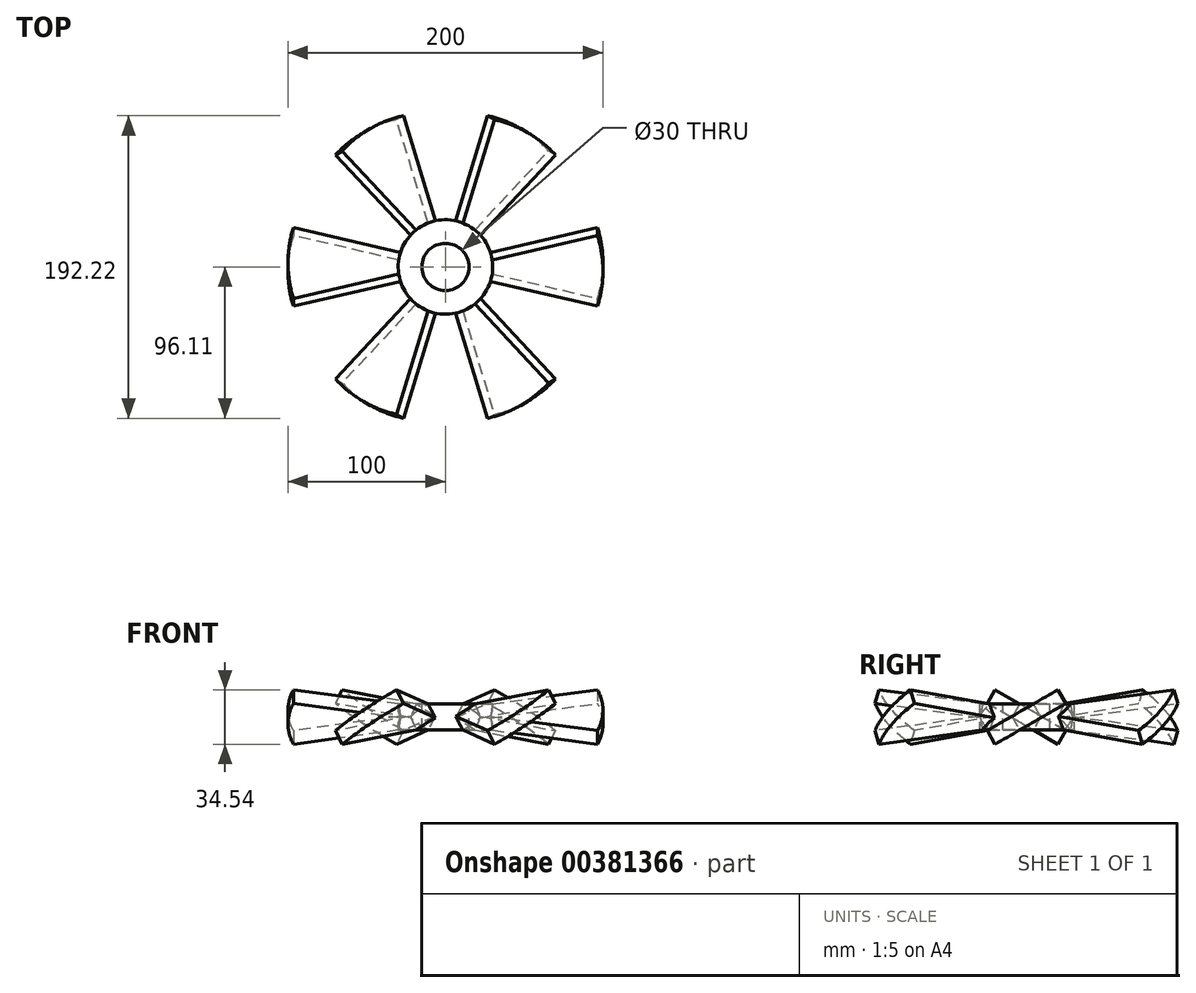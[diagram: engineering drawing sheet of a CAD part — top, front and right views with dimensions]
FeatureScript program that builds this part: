
annotation { "Feature Type Name" : "Feature", "Feature Type Description" : "" }
export const myFeature = defineFeature(function(context is Context, id is Id, definition is map)
    precondition{}
    {
        {
            var Q0;
            Q0=qCreatedBy(makeId("Top.planeOp"),FACE);
            var sketch = newSketch(context, id + "F0", { "sketchPlane" : qUnion([Q0])});
            skLineSegment(sketch, "E0", {"start": v(0, 0) * mm, "end": v(96.6, -25.88) * mm});
            skArc(sketch, "E1", {"start": v(96.6, -25.88) * mm, "mid": v(100, 0) * mm, "end": v(96.6, 25.88) * mm});
            skLineSegment(sketch, "E2", {"start": v(-21.82, 0) * mm, "end": v(117.57, 0) * mm, "construction": true});
            skLineSegment(sketch, "E3.MirrorCS", {"start": v(0, 0) * mm, "end": v(96.6, 25.88) * mm});
            skSolve(sketch);
        }
        {
            var Q0;
            Q0=makeQuery(id+"F0.imprint","IMPRINT",FACE,{"disambiguationData":[TD([[makeQuery(id+"F0.imprint","IMPRINT",EDGE,{"derivedFrom":sQuery(id+"F0.wireOp",EDGE,"E0")}),1.0]])]});
            extrude(context, id + "F1", {"entities" : qUnion([Q0]), "depth" : 5 * mm, "hasSecondDirection" : true, "secondDirectionOppositeDirection" : true, "secondDirectionDepth" : 5 * mm});
        }
        {
            var Q0;
            Q0=qCreatedBy(makeId("Top.planeOp"),FACE);
            var sketch = newSketch(context, id + "F2", { "sketchPlane" : qUnion([Q0])});
            skLineSegment(sketch, "E4", {"start": v(-12.3, 0) * mm, "end": v(109.83, 0) * mm, "construction": true});
            skSolve(sketch);
        }
        {
            var Q0;
            Q0=makeQuery(id+"F1.opExtrude","SWEPT_BODY",BODY,{"disambiguationData":[OSD([sQuery(id+"F0.wireOp",EDGE,"E0"),sQuery(id+"F0.wireOp",EDGE,"E1"),sQuery(id+"F0.wireOp",EDGE,"E3.MirrorCS")])]});
            var Q1;
            Q1=sQuery(id+"F2.wireOp",EDGE,"E4");
            var Q2;
            Q2=sQuery(id+"F2.wireOp",EDGE,"E4");
            transform(context, id + "F3", {"entities" : qUnion([Q0]), "transformType" : TransformType.ROTATION, "transformAxis" : qUnion([Q2]), "angle" : 30 * degree, "makeCopy" : false});
        }
        {
            var Q0;
            Q0=qCreatedBy(makeId("Right.planeOp"),FACE);
            var sketch = newSketch(context, id + "F4", { "sketchPlane" : qUnion([Q0])});
            skLineSegment(sketch, "E5", {"start": v(0, 0) * mm, "end": v(0, 57.38) * mm, "construction": true});
            skSolve(sketch);
        }
        {
            var Q0;
            Q0=makeQuery(id+"F1.opExtrude","SWEPT_BODY",BODY,{"disambiguationData":[OSD([sQuery(id+"F0.wireOp",EDGE,"E0"),sQuery(id+"F0.wireOp",EDGE,"E1"),sQuery(id+"F0.wireOp",EDGE,"E3.MirrorCS")])]});
            var Q1;
            Q1=sQuery(id+"F4.wireOp",EDGE,"E5");
            circularPattern(context, id + "F5", {"entities" : qUnion([Q0]), "axis" : qUnion([Q1]), "angle" : 360 * degree, "instanceCount" : 6, "equalSpace" : true});
        }
        {
            var Q0;
            Q0=qCreatedBy(makeId("Top.planeOp"),FACE);
            var sketch = newSketch(context, id + "F6", { "sketchPlane" : qUnion([Q0])});
            skCircle(sketch, "E6", {"center": v(0, 0) * mm, "radius": 30 * mm});
            skSolve(sketch);
        }
        {
            var Q0;
            Q0=makeQuery(id+"F6.imprint","IMPRINT",FACE,{"disambiguationData":[TD([[makeQuery(id+"F6.imprint","IMPRINT",EDGE,{"derivedFrom":sQuery(id+"F6.wireOp",EDGE,"E6")}),1.0]])]});
            var Q1;
            Q1=sQuery(id+"F6.wireOp",EDGE,"E6");
            extrude(context, id + "F7", {"entities" : qUnion([Q0]), "surfaceEntities" : qUnion([Q1]), "depth" : 25 * mm, "hasSecondDirection" : true, "secondDirectionOppositeDirection" : true, "secondDirectionDepth" : 25 * mm});
        }
        {
            var Q0;
            Q0=makeQuery(id+"F5.opPattern","COPY",BODY,{"derivedFrom":makeQuery(id+"F1.opExtrude","SWEPT_BODY",BODY,{"disambiguationData":[OSD([sQuery(id+"F0.wireOp",EDGE,"E0"),sQuery(id+"F0.wireOp",EDGE,"E1"),sQuery(id+"F0.wireOp",EDGE,"E3.MirrorCS")])]}),"instanceName":"1"});
            var Q1;
            Q1=makeQuery(id+"F5.opPattern","COPY",BODY,{"derivedFrom":makeQuery(id+"F1.opExtrude","SWEPT_BODY",BODY,{"disambiguationData":[OSD([sQuery(id+"F0.wireOp",EDGE,"E0"),sQuery(id+"F0.wireOp",EDGE,"E1"),sQuery(id+"F0.wireOp",EDGE,"E3.MirrorCS")])]}),"instanceName":"3"});
            var Q2;
            Q2=makeQuery(id+"F5.opPattern","COPY",BODY,{"derivedFrom":makeQuery(id+"F1.opExtrude","SWEPT_BODY",BODY,{"disambiguationData":[OSD([sQuery(id+"F0.wireOp",EDGE,"E0"),sQuery(id+"F0.wireOp",EDGE,"E1"),sQuery(id+"F0.wireOp",EDGE,"E3.MirrorCS")])]}),"instanceName":"5"});
            var Q3;
            Q3=makeQuery(id+"F5.opPattern","COPY",BODY,{"derivedFrom":makeQuery(id+"F1.opExtrude","SWEPT_BODY",BODY,{"disambiguationData":[OSD([sQuery(id+"F0.wireOp",EDGE,"E0"),sQuery(id+"F0.wireOp",EDGE,"E1"),sQuery(id+"F0.wireOp",EDGE,"E3.MirrorCS")])]}),"instanceName":"2"});
            var Q4;
            Q4=makeQuery(id+"F5.opPattern","COPY",BODY,{"derivedFrom":makeQuery(id+"F1.opExtrude","SWEPT_BODY",BODY,{"disambiguationData":[OSD([sQuery(id+"F0.wireOp",EDGE,"E0"),sQuery(id+"F0.wireOp",EDGE,"E1"),sQuery(id+"F0.wireOp",EDGE,"E3.MirrorCS")])]}),"instanceName":"4"});
            var Q5;
            Q5=makeQuery(id+"F1.opExtrude","SWEPT_BODY",BODY,{"disambiguationData":[OSD([sQuery(id+"F0.wireOp",EDGE,"E0"),sQuery(id+"F0.wireOp",EDGE,"E1"),sQuery(id+"F0.wireOp",EDGE,"E3.MirrorCS")])]});
            var Q6;
            Q6=makeQuery(id+"F7.opExtrude","SWEPT_BODY",BODY,{"disambiguationData":[OSD([sQuery(id+"F6.wireOp",EDGE,"E6")])]});
            booleanBodies(context, id + "F8", {"operationType" : BooleanOperationType.UNION, "tools" : qUnion([Q0, Q1, Q2, Q3, Q4, Q5, Q6])});
        }
        {
            var Q0;
            {var subQ0=sQuery(id+"F0.wireOp",EDGE,"E0");Q0=makeQuery(id+"F8.opBoolean","INTERSECT",VERTEX,{"derivedFrom":[makeQuery(id+"F5.opPattern","COPY",FACE,{"derivedFrom":makeQuery(id+"F1.opExtrude","SWEPT_FACE",FACE,{"disambiguationData":[OSD([subQ0])]}),"instanceName":"1"}),makeQuery(id+"F5.opPattern","COPY",FACE,{"derivedFrom":makeQuery(id+"F1.opExtrude","CAP_FACE",FACE,{"disambiguationData":[OSD([subQ0,sQuery(id+"F0.wireOp",EDGE,"E1"),sQuery(id+"F0.wireOp",EDGE,"E3.MirrorCS")])],"isStart":true}),"instanceName":"1"}),makeQuery(id+"F7.opExtrude","SWEPT_FACE",FACE,{"disambiguationData":[OSD([sQuery(id+"F6.wireOp",EDGE,"E6")])]})]});}
            var Q1;
            {var subQ0=sQuery(id+"F0.wireOp",EDGE,"E0");Q1=makeQuery(id+"F8.opBoolean","INTERSECT",VERTEX,{"derivedFrom":[makeQuery(id+"F5.opPattern","COPY",FACE,{"derivedFrom":makeQuery(id+"F1.opExtrude","SWEPT_FACE",FACE,{"disambiguationData":[OSD([subQ0])]}),"instanceName":"5"}),makeQuery(id+"F5.opPattern","COPY",FACE,{"derivedFrom":makeQuery(id+"F1.opExtrude","CAP_FACE",FACE,{"disambiguationData":[OSD([subQ0,sQuery(id+"F0.wireOp",EDGE,"E1"),sQuery(id+"F0.wireOp",EDGE,"E3.MirrorCS")])],"isStart":true}),"instanceName":"5"}),makeQuery(id+"F7.opExtrude","SWEPT_FACE",FACE,{"disambiguationData":[OSD([sQuery(id+"F6.wireOp",EDGE,"E6")])]})]});}
            var Q2;
            {var subQ0=sQuery(id+"F0.wireOp",EDGE,"E0");Q2=makeQuery(id+"F8.opBoolean","INTERSECT",VERTEX,{"derivedFrom":[makeQuery(id+"F5.opPattern","COPY",FACE,{"derivedFrom":makeQuery(id+"F1.opExtrude","SWEPT_FACE",FACE,{"disambiguationData":[OSD([subQ0])]}),"instanceName":"3"}),makeQuery(id+"F5.opPattern","COPY",FACE,{"derivedFrom":makeQuery(id+"F1.opExtrude","CAP_FACE",FACE,{"disambiguationData":[OSD([subQ0,sQuery(id+"F0.wireOp",EDGE,"E1"),sQuery(id+"F0.wireOp",EDGE,"E3.MirrorCS")])],"isStart":true}),"instanceName":"3"}),makeQuery(id+"F7.opExtrude","SWEPT_FACE",FACE,{"disambiguationData":[OSD([sQuery(id+"F6.wireOp",EDGE,"E6")])]})]});}
            cPlane(context, id + "F9", {"entities" : qUnion([Q0, Q1, Q2]), "cplaneType" : CPlaneType.THREE_POINT, "offset" : 25 * mm, "width" : 150 * mm, "height" : 150 * mm});
        }
        {
            var Q0;
            {var subQ0=sQuery(id+"F0.wireOp",EDGE,"E3.MirrorCS");Q0=makeQuery(id+"F8.opBoolean","INTERSECT",VERTEX,{"derivedFrom":[makeQuery(id+"F1.opExtrude","CAP_FACE",FACE,{"disambiguationData":[OSD([sQuery(id+"F0.wireOp",EDGE,"E0"),sQuery(id+"F0.wireOp",EDGE,"E1"),subQ0])],"isStart":false}),makeQuery(id+"F1.opExtrude","SWEPT_FACE",FACE,{"disambiguationData":[OSD([subQ0])]}),makeQuery(id+"F7.opExtrude","SWEPT_FACE",FACE,{"disambiguationData":[OSD([sQuery(id+"F6.wireOp",EDGE,"E6")])]})]});}
            var Q1;
            {var subQ0=sQuery(id+"F0.wireOp",EDGE,"E3.MirrorCS");Q1=makeQuery(id+"F8.opBoolean","INTERSECT",VERTEX,{"derivedFrom":[makeQuery(id+"F5.opPattern","COPY",FACE,{"derivedFrom":makeQuery(id+"F1.opExtrude","CAP_FACE",FACE,{"disambiguationData":[OSD([sQuery(id+"F0.wireOp",EDGE,"E0"),sQuery(id+"F0.wireOp",EDGE,"E1"),subQ0])],"isStart":false}),"instanceName":"1"}),makeQuery(id+"F5.opPattern","COPY",FACE,{"derivedFrom":makeQuery(id+"F1.opExtrude","SWEPT_FACE",FACE,{"disambiguationData":[OSD([subQ0])]}),"instanceName":"1"}),makeQuery(id+"F7.opExtrude","SWEPT_FACE",FACE,{"disambiguationData":[OSD([sQuery(id+"F6.wireOp",EDGE,"E6")])]})]});}
            var Q2;
            {var subQ0=sQuery(id+"F0.wireOp",EDGE,"E3.MirrorCS");Q2=makeQuery(id+"F8.opBoolean","INTERSECT",VERTEX,{"derivedFrom":[makeQuery(id+"F5.opPattern","COPY",FACE,{"derivedFrom":makeQuery(id+"F1.opExtrude","CAP_FACE",FACE,{"disambiguationData":[OSD([sQuery(id+"F0.wireOp",EDGE,"E0"),sQuery(id+"F0.wireOp",EDGE,"E1"),subQ0])],"isStart":false}),"instanceName":"3"}),makeQuery(id+"F5.opPattern","COPY",FACE,{"derivedFrom":makeQuery(id+"F1.opExtrude","SWEPT_FACE",FACE,{"disambiguationData":[OSD([subQ0])]}),"instanceName":"3"}),makeQuery(id+"F7.opExtrude","SWEPT_FACE",FACE,{"disambiguationData":[OSD([sQuery(id+"F6.wireOp",EDGE,"E6")])]})]});}
            cPlane(context, id + "F10", {"entities" : qUnion([Q0, Q1, Q2]), "cplaneType" : CPlaneType.THREE_POINT, "offset" : 25 * mm, "width" : 150 * mm, "height" : 150 * mm});
        }
        {
            var Q0;
            Q0=makeQuery(id+"F7.opExtrude","CAP_FACE",FACE,{"disambiguationData":[OSD([sQuery(id+"F6.wireOp",EDGE,"E6")])],"isStart":true});
            var Q1;
            Q1=qCreatedBy(id+"F9.planeOp",FACE);
            extrude(context, id + "F11", {"entities" : qUnion([Q0]), "operationType" : NewBodyOperationType.REMOVE, "endBound" : BoundingType.UP_TO_SURFACE, "oppositeDirection" : true, "endBoundEntityFace" : qUnion([Q1]), "depth" : 25 * mm});
        }
        {
            var Q0;
            Q0=makeQuery(id+"F7.opExtrude","CAP_FACE",FACE,{"disambiguationData":[OSD([sQuery(id+"F6.wireOp",EDGE,"E6")])],"isStart":false});
            var Q1;
            Q1=qCreatedBy(id+"F10.planeOp",FACE);
            extrude(context, id + "F12", {"entities" : qUnion([Q0]), "operationType" : NewBodyOperationType.REMOVE, "endBound" : BoundingType.UP_TO_SURFACE, "oppositeDirection" : true, "endBoundEntityFace" : qUnion([Q1]), "depth" : 25 * mm});
        }
        {
            var Q0;
            Q0=makeQuery(id+"F12.boolean.opBoolean","COPY",FACE,{"derivedFrom":makeQuery(id+"F12.opExtrude","CAP_FACE",FACE,{"disambiguationData":[OSD([sQuery(id+"F6.wireOp",EDGE,"E6")])],"isStart":false})});
            var sketch = newSketch(context, id + "F13", { "sketchPlane" : qUnion([Q0])});
            skCircle(sketch, "E7", {"center": v(0, 0) * mm, "radius": 15 * mm});
            skSolve(sketch);
        }
        {
            var Q0;
            Q0=makeQuery(id+"F13.imprint","IMPRINT",FACE,{"disambiguationData":[TD([[makeQuery(id+"F13.imprint","IMPRINT",EDGE,{"derivedFrom":sQuery(id+"F13.wireOp",EDGE,"E7")}),1.0]])]});
            extrude(context, id + "F14", {"entities" : qUnion([Q0]), "operationType" : NewBodyOperationType.REMOVE, "endBound" : BoundingType.UP_TO_NEXT, "oppositeDirection" : true, "depth" : 25 * mm});
        }
    });
